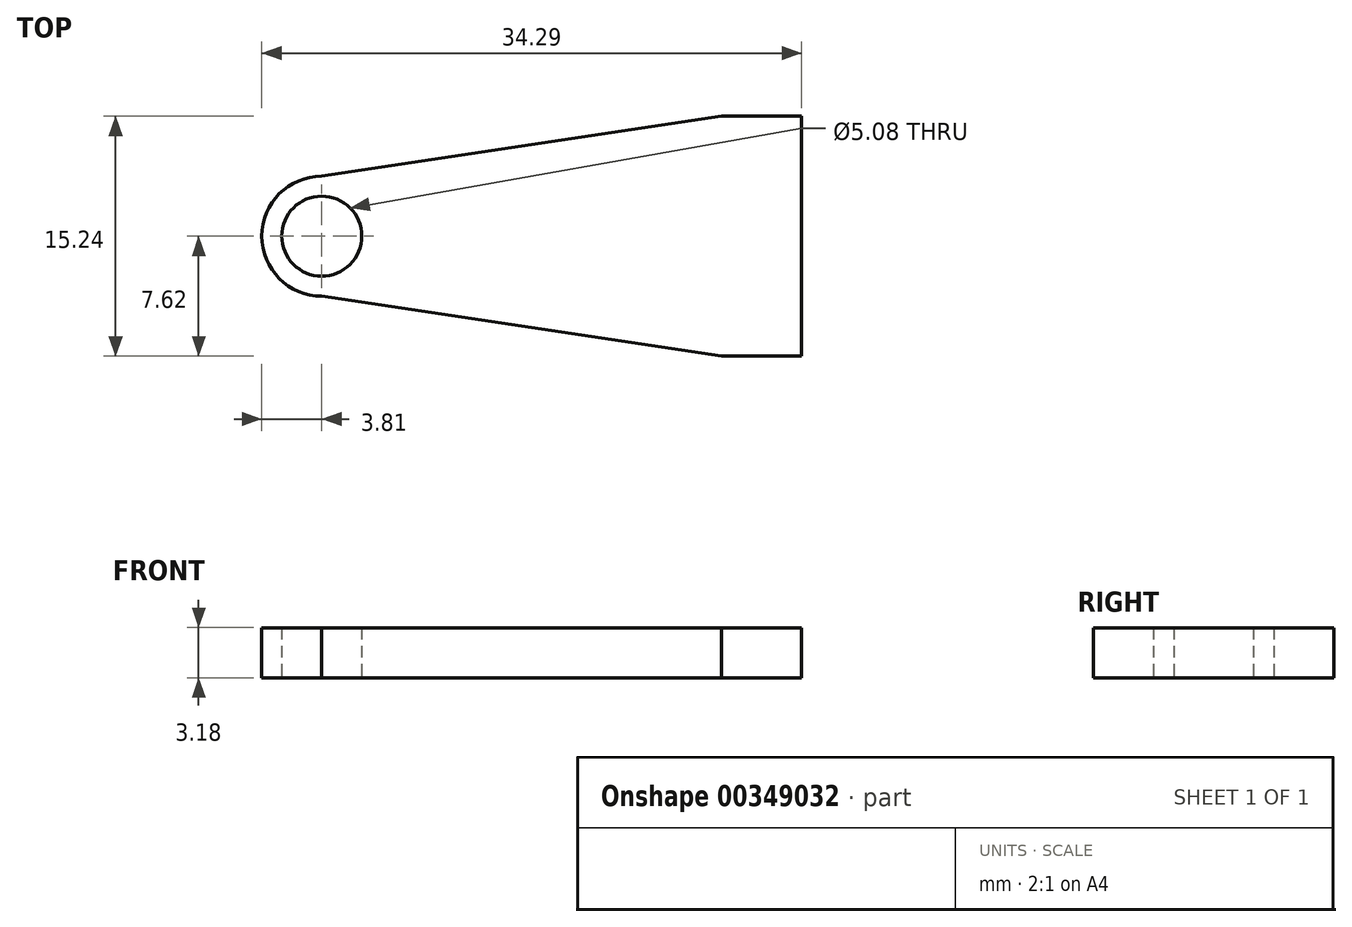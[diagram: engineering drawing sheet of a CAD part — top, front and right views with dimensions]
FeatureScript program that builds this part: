
annotation { "Feature Type Name" : "Feature", "Feature Type Description" : "" }
export const myFeature = defineFeature(function(context is Context, id is Id, definition is map)
    precondition{}
    {
        {
            var Q0;
            Q0=qCreatedBy(makeId("Top.planeOp"),FACE);
            var sketch = newSketch(context, id + "F0", { "sketchPlane" : qUnion([Q0])});
            skArc(sketch, "E0", {"start": v(0, 3.81) * mm, "mid": v(-3.81, 0) * mm, "end": v(0, -3.81) * mm});
            skLineSegment(sketch, "E1", {"start": v(0, 3.8) * mm, "end": v(25.4, 7.62) * mm});
            skLineSegment(sketch, "E2", {"start": v(0, -3.8) * mm, "end": v(25.4, -7.62) * mm});
            skLineSegment(sketch, "E3", {"start": v(25.4, 7.62) * mm, "end": v(30.48, 7.62) * mm});
            skLineSegment(sketch, "E4", {"start": v(25.4, -7.62) * mm, "end": v(30.48, -7.62) * mm});
            skLineSegment(sketch, "E5", {"start": v(30.48, 7.62) * mm, "end": v(30.48, -7.62) * mm});
            skSolve(sketch);
        }
        {
            var Q0;
            Q0=makeQuery(id+"F0.imprint","IMPRINT",FACE,{"disambiguationData":[TD([[makeQuery(id+"F0.imprint","IMPRINT",EDGE,{"derivedFrom":sQuery(id+"F0.wireOp",EDGE,"E0")}),1.0]])]});
            extrude(context, id + "F1", {"entities" : qUnion([Q0]), "depth" : 3.17 * mm});
        }
        {
            var Q0;
            Q0=makeQuery(id+"F1.opExtrude","CAP_FACE",FACE,{"disambiguationData":[OSD([sQuery(id+"F0.wireOp",EDGE,"E0"),sQuery(id+"F0.wireOp",EDGE,"E1"),sQuery(id+"F0.wireOp",EDGE,"E2"),sQuery(id+"F0.wireOp",EDGE,"E3"),sQuery(id+"F0.wireOp",EDGE,"E4"),sQuery(id+"F0.wireOp",EDGE,"E5")])],"isStart":true});
            var sketch = newSketch(context, id + "F2", { "sketchPlane" : qUnion([Q0])});
            skPoint(sketch, "E6", {"position": v(0, 0) * mm});
            skSolve(sketch);
        }
        {
            var Q0;
            Q0=sQuery(id+"F2.wireOp",VERTEX,"E6");
            var Q1;
            Q1=makeQuery(id+"F1.opExtrude","SWEPT_BODY",BODY,{"disambiguationData":[OSD([sQuery(id+"F0.wireOp",EDGE,"E0"),sQuery(id+"F0.wireOp",EDGE,"E1"),sQuery(id+"F0.wireOp",EDGE,"E2"),sQuery(id+"F0.wireOp",EDGE,"E3"),sQuery(id+"F0.wireOp",EDGE,"E4"),sQuery(id+"F0.wireOp",EDGE,"E5")])]});
            hole(context, id + "F3", {"style" : HoleStyle.SIMPLE, "endStyle" : HoleEndStyle.THROUGH, "holeDiameter" : 5.08 * mm, "isTappedThrough" : true, "tappedDepth" : 12.7 * mm, "tapClearance" : 3, "locations" : qUnion([Q0]), "scope" : qUnion([Q1])});
        }
    });
